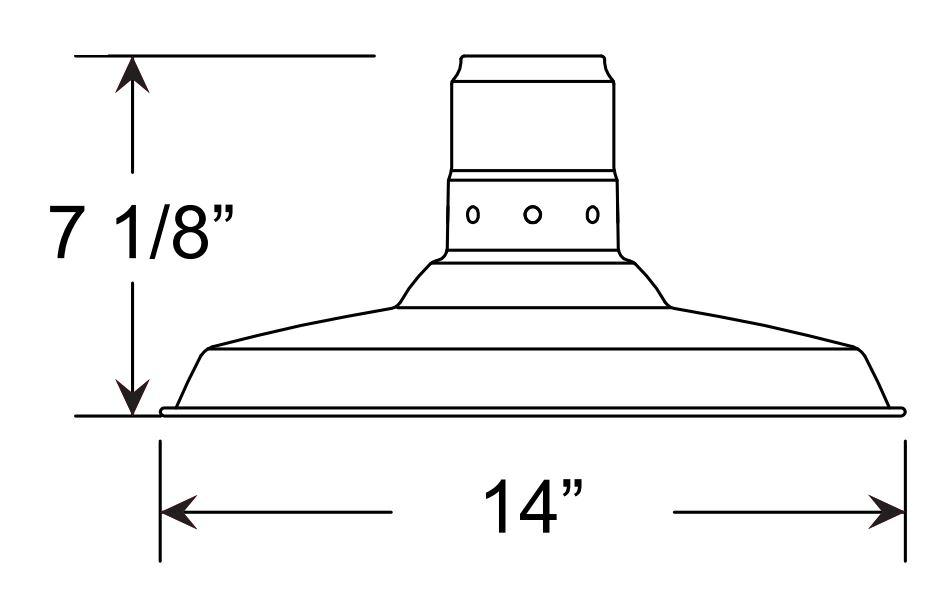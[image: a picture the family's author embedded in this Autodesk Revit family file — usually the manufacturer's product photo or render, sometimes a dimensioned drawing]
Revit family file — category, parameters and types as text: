
# Revit family: Azalea(12,16,20,24)MB
name_source: partatom
category: Lighting Fixtures
units: mm (PartAtom-declared; Revit-internal decimal feet)

## family parameters
Always vertical = Yes
Cut with Voids When Loaded = No
Light Source = Yes
OmniClass Number = 23.80.70.00
OmniClass Title = Lighting
Part Type = Normal
Room Calculation Point = No
Round Connector Dimension = Use Diameter
Shared = No
Work Plane-Based = No

## types (4) — shared parameters
Apparent Load = 60 VA
Body Colour = Spun aluminium
Body Material = body
CRI = >90
Color Filter = 16777215
Construction Material = Heavy Duty spun aluminum.
Default Elevation = 0' - 0"
Description = 120-277 Voltage
Dimming = 1%
Dimming Lamp Color Temperature Shift = <None>
Efficiency = 65-125 lumens per watt
Fixture Finish = Fixture finish
GLASS = Glass
Lamp = MB
Life = L70 50,000 hours
Load Classification = Lighting
Manufacturer = ANP Lighting
Power Factor = 1
Tilt Angle = 90.00°
URL = https://www.anplighting.com
Voltage = 277 V
Warranty = 5 year limited warranty
Wattage Comments = 60W Max

## per-type parameters (varying)
| type | Fixture Diameter | Fixture Height | MDA12 | MDA16 | MDA20 | MDA24 | Photometric Web File | Weight |
| MDA12 | 1' - 0" | 0' - 9 1/2" | Yes | No | No | No | MDA12M010LD35K.IES | 3.0lbs |
| MDA16 | 1' - 0" | 0' - 9 1/2" | No | Yes | No | No | MDA16M016LD35K.IES | 3.5lbs |
| MDA20 | 1' - 8" | 1' - 4" | No | No | Yes | No | MDA20M016LD35K.IES | 4.0lbs |
| MDA24 | 2' - 0" | 1' - 7" | No | No | No | Yes | MDA24M024LD35K.IES | 4.5lbs |

note: column(s) folded — value = type name in every type: Model

## geometry (parser evidence)
native form markers: Sweep x33
no freeform markers — native parametric forms only
